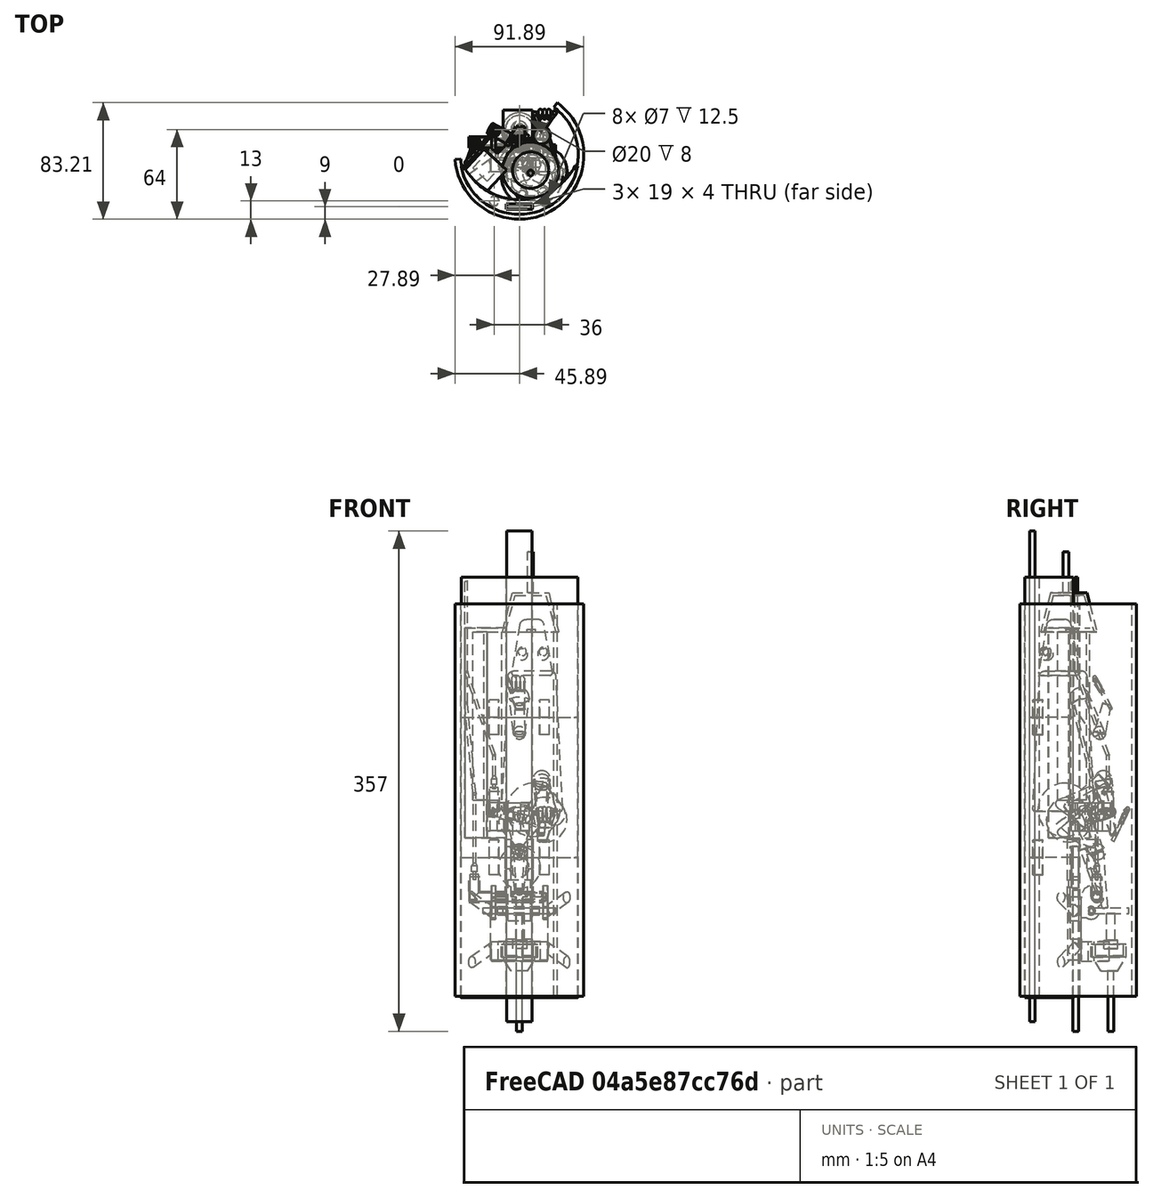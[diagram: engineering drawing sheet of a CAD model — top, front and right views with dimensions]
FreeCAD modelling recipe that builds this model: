
FCSTD DOCUMENT  (FreeCAD 0.19R17499 (Git))
Label: modele3.0
License: All rights reserved
LicenseURL: http://en.wikipedia.org/wiki/All_rights_reserved
objects: Part::Cylinder×80, Part::Cut×43, Part::Fuse×42, Part::Box×31, Part::Cone×19, Part::Sphere×19, Part::Fillet×16, Part::Mirroring×8, Part::MultiFuse×3, Drawing::FeatureViewPart×2, Drawing::FeaturePage×1
note: 261 computed .brp shape members not serialized (recipe doc carries the construction recipe); baked Part::Feature solids carry a one-line shape summary decoded from their .brp

FEATURE [Part::Cylinder] Cylinder  label="Cylindre"
  Angle = 360
  AttacherType = Attacher::AttachEngine3D
  Height = 100
  Radius = 42.5
FEATURE [Part::Cylinder] Cylinder001  label="Cylindre001"
  Angle = 360
  AttacherType = Attacher::AttachEngine3D
  Height = 100
  Placement = pos=(0,13,0) rot=(0,0,1;0rad)
  Radius = 45
FEATURE [Part::Cut] Cut
  Base = -> Cylinder
  Tool = -> Cylinder001
FEATURE [Part::Fillet] Fillet
  Base = -> Cut
  Edges = 1 edges r=1: [Edge4]
FEATURE [Part::Fillet] Fillet001
  Base = -> Fillet
  Edges = 1 edges r=1: [Edge3]
FEATURE [Part::Box] Box  label="Cube"
  AttacherType = Attacher::AttachEngine3D
  Height = 100
  Length = 19
  Placement = pos=(-9.5,-39,0) rot=(0,0,1;0rad)
  Width = 4
FEATURE [Part::Cut] Cut001  label="Support 1"
  Base = -> Fillet001
  Tool = -> Box
FEATURE [Part::Cylinder] Cylinder002  label="Cylindre002"
  Angle = 360
  AttacherType = Attacher::AttachEngine3D
  Height = 100
  Placement = pos=(0,13,0) rot=(0,0,1;0rad)
  Radius = 45
FEATURE [Part::Cylinder] Cylinder003  label="Cylindre003"
  Angle = 360
  AttacherType = Attacher::AttachEngine3D
  Height = 100
  Radius = 42.5
FEATURE [Part::Box] Box001  label="Cube001"
  AttacherType = Attacher::AttachEngine3D
  Height = 100
  Length = 19
  Placement = pos=(-9.5,-39,0) rot=(0,0,1;0rad)
  Width = 4
FEATURE [Part::Cut] Cut003
  Base = -> Cylinder003
  Tool = -> Cylinder002
FEATURE [Part::Fillet] Fillet003
  Base = -> Cut003
  Edges = 1 edges r=1: [Edge4]
FEATURE [Part::Fillet] Fillet002
  Base = -> Fillet003
  Edges = 1 edges r=1: [Edge3]
FEATURE [Part::Cut] Cut002  label="Support 2"
  Base = -> Fillet002
  Placement = pos=(0,0,-100) rot=(0,0,1;0rad)
  Tool = -> Box001
FEATURE [Part::Cylinder] Cylinder004  label="Cylindre004"
  Angle = 360
  AttacherType = Attacher::AttachEngine3D
  Height = 100
  Placement = pos=(0,13,0) rot=(0,0,1;0rad)
  Radius = 45
FEATURE [Part::Cylinder] Cylinder005  label="Cylindre005"
  Angle = 360
  AttacherType = Attacher::AttachEngine3D
  Height = 100
  Radius = 42.5
FEATURE [Part::Box] Box002  label="Cube002"
  AttacherType = Attacher::AttachEngine3D
  Height = 100
  Length = 19
  Placement = pos=(-9.5,-39,0) rot=(0,0,1;0rad)
  Width = 4
FEATURE [Part::Cut] Cut005
  Base = -> Cylinder005
  Tool = -> Cylinder004
FEATURE [Part::Fillet] Fillet005
  Base = -> Cut005
  Edges = 1 edges r=1: [Edge4]
FEATURE [Part::Fillet] Fillet004
  Base = -> Fillet005
  Edges = 1 edges r=1: [Edge3]
FEATURE [Part::Cut] Cut004  label="Support pedale"
  Base = -> Fillet004
  Placement = pos=(0,0,-200) rot=(0,0,1;0rad)
  Tool = -> Box002
FEATURE [Part::Cylinder] Cylinder006  label="Cylindre006"
  Angle = 360
  AttacherType = Attacher::AttachEngine3D
  Height = 25
  Placement = pos=(-18,-33,-12.5) rot=(0,0,1;0rad)
  Radius = 3.5
FEATURE [Part::Cylinder] Cylinder007  label="Cylindre007"
  Angle = 360
  AttacherType = Attacher::AttachEngine3D
  Height = 25
  Placement = pos=(-18,-33,-12.5) rot=(0,0,1;0rad)
  Radius = 3.5
FEATURE [Part::Cut] Cut006
  Base = -> Cut001
  Tool = -> Cylinder006
FEATURE [Part::Cut] Cut007
  Base = -> Cut002
  Tool = -> Cylinder007
FEATURE [Part::Cylinder] Cylinder009  label="Cylindre009"
  Angle = 360
  AttacherType = Attacher::AttachEngine3D
  Height = 25
  Placement = pos=(18,-33,-12.5) rot=(0,0,1;0rad)
  Radius = 3.5
FEATURE [Part::Cylinder] Cylinder010  label="Cylindre010"
  Angle = 360
  AttacherType = Attacher::AttachEngine3D
  Height = 25
  Placement = pos=(18,-33,-12.5) rot=(0,0,1;0rad)
  Radius = 3.5
FEATURE [Part::Cut] Cut008  label="Support 2 "
  Base = -> Cut007
  Tool = -> Cylinder009
FEATURE [Part::Cut] Cut009  label="Support 1 "
  Base = -> Cut006
  Tool = -> Cylinder010
FEATURE [Part::Cylinder] Cylinder011  label="Ergot 1"
  Angle = 360
  AttacherType = Attacher::AttachEngine3D
  Height = 25
  Placement = pos=(18,-33,-12.5) rot=(0,0,1;0rad)
  Radius = 3.3
FEATURE [Part::Cylinder] Cylinder012  label="Ergot 2"
  Angle = 360
  AttacherType = Attacher::AttachEngine3D
  Height = 25
  Placement = pos=(-18,-33,-12.5) rot=(0,0,1;0rad)
  Radius = 3.3
FEATURE [Part::Cylinder] Cylinder014  label="Cylindre012"
  Angle = 360
  AttacherType = Attacher::AttachEngine3D
  Height = 25
  Placement = pos=(-18,-33,-112.5) rot=(0,0,1;0rad)
  Radius = 3.5
FEATURE [Part::Cylinder] Cylinder015  label="Cylindre013"
  Angle = 360
  AttacherType = Attacher::AttachEngine3D
  Height = 25
  Placement = pos=(18,-33,-112.5) rot=(0,0,1;0rad)
  Radius = 3.5
FEATURE [Part::Cylinder] Cylinder016  label="Cylindre014"
  Angle = 360
  AttacherType = Attacher::AttachEngine3D
  Height = 25
  Placement = pos=(-18,-33,-112.5) rot=(0,0,1;0rad)
  Radius = 3.5
FEATURE [Part::Cylinder] Cylinder017  label="Cylindre015"
  Angle = 360
  AttacherType = Attacher::AttachEngine3D
  Height = 25
  Placement = pos=(18,-33,-112.5) rot=(0,0,1;0rad)
  Radius = 3.5
FEATURE [Part::Cut] Cut010
  Base = -> Cut008
  Tool = -> Cylinder016
FEATURE [Part::Cut] Cut011  label="Support 2 001"
  Base = -> Cut010
  Tool = -> Cylinder017
FEATURE [Part::Cut] Cut012
  Base = -> Cut004
  Tool = -> Cylinder014
FEATURE [Part::Cut] Cut013
  Base = -> Cut012
  Tool = -> Cylinder015
FEATURE [Part::Cylinder] Cylinder018  label="Ergot 3"
  Angle = 360
  AttacherType = Attacher::AttachEngine3D
  Height = 25
  Placement = pos=(18,-33,-112.5) rot=(0,0,1;0rad)
  Radius = 3.3
FEATURE [Part::Cylinder] Cylinder019  label="Ergot 4"
  Angle = 360
  AttacherType = Attacher::AttachEngine3D
  Height = 25
  Placement = pos=(-18,-33,-112.5) rot=(0,0,1;0rad)
  Radius = 3.3
FEATURE [Part::Box] Box003  label="Cube003"
  AttacherType = Attacher::AttachEngine3D
  Height = 45
  Length = 41
  Placement = pos=(-20.5,-12,-173) rot=(0,0,1;0rad)
  Width = 10
FEATURE [Part::Cylinder] Cylinder020  label="Cylindre016"
  Angle = 360
  AttacherType = Attacher::AttachEngine3D
  Height = 24
  Placement = pos=(-36,-18,-176) rot=(0,0.707107,0.707107;1.5708rad)
  Radius = 3.5
FEATURE [Part::Mirroring] Part__Mirroring  label="Cylindre016 (Mirror #1)"
  Base = (0,0,0)
  Normal = (0,0,1)
  Placement = pos=(0,0,-303) rot=(0,0,1;0rad)
  Source = -> Cylinder020
FEATURE [Part::Mirroring] Part__Mirroring001  label="Cylindre016 (Mirror #2)"
  Base = (0,0,0)
  Normal = (1,0,0)
  Source = -> Cylinder020
FEATURE [Part::Mirroring] Part__Mirroring002  label="Cylindre016 (Mirror #3)"
  Base = (0,0,0)
  Normal = (1,0,0)
  Source = -> Part__Mirroring
FEATURE [Part::Fuse] Fusion
  Base = -> Box003
  Tool = -> Cylinder020
FEATURE [Part::Fuse] Fusion001
  Base = -> Part__Mirroring
  Tool = -> Fusion
FEATURE [Part::Fuse] Fusion002
  Base = -> Part__Mirroring002
  Tool = -> Fusion001
FEATURE [Part::Fuse] Fusion003
  Base = -> Part__Mirroring001
  Tool = -> Fusion002
FEATURE [Part::Fuse] Fusion004
  Base = -> Cut013
  Tool = -> Fusion003
FEATURE [Part::Cylinder] Cylinder021  label="Cylindre017"
  Angle = 360
  AttacherType = Attacher::AttachEngine3D
  Height = 30
  Placement = pos=(-13,6,-138) rot=(0,1,0;1.5708rad)
  Radius = 3
FEATURE [Part::Box] Box004  label="Cube004"
  AttacherType = Attacher::AttachEngine3D
  Height = 30
  Length = 18
  Placement = pos=(-9,-10,-158) rot=(0,0,1;0rad)
  Width = 8
FEATURE [Part::Cut] Cut014
  Base = -> Fusion004
  Tool = -> Box004
FEATURE [Part::Box] Box005  label="Cube005"
  AttacherType = Attacher::AttachEngine3D
  Height = 51
  Length = 5
  Placement = pos=(-2.5,-14,-174) rot=(0,0,1;0rad)
  Width = 14
FEATURE [Part::Cut] Cut015
  Base = -> Cut014
  Tool = -> Box005
FEATURE [Part::Cylinder] Cylinder022  label="Cylindre018"
  Angle = 360
  AttacherType = Attacher::AttachEngine3D
  Height = 34
  Placement = pos=(-17,6,-138) rot=(0,1,0;1.5708rad)
  Radius = 7
FEATURE [Part::Cylinder] Cylinder024  label="Cylindre020"
  Angle = 360
  AttacherType = Attacher::AttachEngine3D
  Height = 40
  Placement = pos=(-20,6,-138) rot=(0,1,0;1.5708rad)
  Radius = 6
FEATURE [Part::Cylinder] Cylinder025  label="Cylindre021"
  Angle = 360
  AttacherType = Attacher::AttachEngine3D
  Height = 48
  Placement = pos=(-26,6,-138) rot=(0,1,0;1.5708rad)
  Radius = 2
FEATURE [Part::Cut] Cut017
  Base = -> Cylinder024
  Tool = -> Cylinder025
FEATURE [Part::Cylinder] Cylinder026  label="Cylindre022"
  Angle = 360
  AttacherType = Attacher::AttachEngine3D
  Height = 52
  Placement = pos=(-26,6,-138) rot=(0,1,0;1.5708rad)
  Radius = 1.5
FEATURE [Part::Cut] Cut018
  Base = -> Cut017
  Placement = pos=(0,-1,0) rot=(0,0,1;0rad)
  Tool = -> Cylinder022
FEATURE [Part::Cylinder] Cylinder027  label="Cylindre023"
  Angle = 360
  AttacherType = Attacher::AttachEngine3D
  Height = 34
  Placement = pos=(-17,6,-128) rot=(0,1,0;1.5708rad)
  Radius = 8
FEATURE [Part::Cylinder] Cylinder028  label="Axe pedale"
  Angle = 360
  AttacherType = Attacher::AttachEngine3D
  Height = 52
  Placement = pos=(-26,5,-138) rot=(0,1,0;1.5708rad)
  Radius = 2
FEATURE [Part::Cut] Cut019
  Base = -> Cylinder021
  Placement = pos=(0,-1,0) rot=(0,0,1;0rad)
  Tool = -> Cylinder026
FEATURE [Part::Cylinder] Cylinder029  label="Cylindre025"
  Angle = 360
  AttacherType = Attacher::AttachEngine3D
  Height = 40
  Placement = pos=(-20,6,-128) rot=(0,1,0;1.5708rad)
  Radius = 8
FEATURE [Part::Cut] Cut020
  Base = -> Cylinder029
  Tool = -> Cylinder027
FEATURE [Part::Box] Box006  label="Cube006"
  AttacherType = Attacher::AttachEngine3D
  Height = 4
  Length = 21
  Placement = pos=(-9,7,-140) rot=(0,0,1;0rad)
  Width = 25
FEATURE [Part::Fuse] Fusion005
  Base = -> Cut019
  Tool = -> Box006
FEATURE [Part::Cylinder] Cylinder030  label="Cylindre026"
  Angle = 360
  AttacherType = Attacher::AttachEngine3D
  Height = 52
  Placement = pos=(-26,9,-128) rot=(0,1,0;1.5708rad)
  Radius = 2.5
FEATURE [Part::Cylinder] Cylinder031  label="Cylindre027"
  Angle = 360
  AttacherType = Attacher::AttachEngine3D
  Height = 21
  Placement = pos=(3,19,-161) rot=(0,0,1;0rad)
  Radius = 3
FEATURE [Part::Cylinder] Cylinder032  label="Cylindre028"
  Angle = 360
  AttacherType = Attacher::AttachEngine3D
  Height = 6
  Placement = pos=(3,19,-165) rot=(0,0,1;0rad)
  Radius = 5
FEATURE [Part::Fuse] Fusion006
  Base = -> Fusion005
  Tool = -> Cylinder031
FEATURE [Part::Fuse] Fusion007  label="Pedale"
  Base = -> Cylinder032
  Placement = pos=(-2.5,0,0) rot=(0,0,1;0rad)
  Tool = -> Fusion006
FEATURE [Part::Box] Box007  label="Cube007"
  AttacherType = Attacher::AttachEngine3D
  Height = 14
  Length = 3
  Placement = pos=(17,-2,-143) rot=(0,0,1;0rad)
  Width = 5
FEATURE [Part::Box] Box008  label="Cube008"
  AttacherType = Attacher::AttachEngine3D
  Height = 14
  Length = 3
  Placement = pos=(-20,-2,-143) rot=(0,0,1;0rad)
  Width = 5
FEATURE [Part::Cylinder] Cylinder033  label="Cylindre029"
  Angle = 360
  AttacherType = Attacher::AttachEngine3D
  Height = 52
  Placement = pos=(-26,9,-128) rot=(0,1,0;1.5708rad)
  Radius = 2.5
FEATURE [Part::Cut] Cut021
  Base = -> Cut020
  Tool = -> Cylinder030
FEATURE [Part::Cut] Cut022
  Base = -> Cut021
  Tool = -> Cylinder033
FEATURE [Part::Cylinder] Cylinder034  label="Cylindre030"
  Angle = 360
  AttacherType = Attacher::AttachEngine3D
  Height = 38
  Placement = pos=(-20,9,-128) rot=(0,1,0;1.5708rad)
  Radius = 4
FEATURE [Part::Cylinder] Cylinder035  label="Cylindre031"
  Angle = 360
  AttacherType = Attacher::AttachEngine3D
  Height = 38
  Placement = pos=(-20,9,-128) rot=(0,1,0;1.5708rad)
  Radius = 2.5
FEATURE [Part::Cut] Cut023
  Base = -> Cylinder034
  Tool = -> Cylinder035
FEATURE [Part::Box] Box009  label="Cube009"
  AttacherType = Attacher::AttachEngine3D
  Height = 10
  Length = 34
  Placement = pos=(-17,11,-133) rot=(0,0,1;0rad)
  Width = 5
FEATURE [Part::Cut] Cut024
  Base = -> Cut023
  Tool = -> Box009
FEATURE [Part::Cylinder] Cylinder036  label="Cylindre032"
  Angle = 360
  AttacherType = Attacher::AttachEngine3D
  Height = 10
  Placement = pos=(0,12,-133) rot=(0,0,1;0rad)
  Radius = 4
FEATURE [Part::Cut] Cut025
  Base = -> Cut024
  Tool = -> Cylinder036
FEATURE [Part::Fuse] Fusion008
  Base = -> Cut022
  Tool = -> Cut025
FEATURE [Part::Fuse] Fusion009
  Base = -> Cut018
  Tool = -> Fusion008
FEATURE [Part::Fuse] Fusion010
  Base = -> Box007
  Tool = -> Fusion009
FEATURE [Part::Fuse] Fusion011
  Base = -> Box008
  Tool = -> Fusion010
FEATURE [Part::Fuse] Fusion012
  Base = -> Cut015
  Tool = -> Fusion011
FEATURE [Part::Cylinder] Cylinder037  label="Cylindre033"
  Angle = 360
  AttacherType = Attacher::AttachEngine3D
  Height = 18
  Placement = pos=(-36,9,-128) rot=(0,1,0;1.5708rad)
  Radius = 4
FEATURE [Part::Cylinder] Cylinder038  label="Cylindre034"
  Angle = 360
  AttacherType = Attacher::AttachEngine3D
  Height = 18
  Placement = pos=(-36,9,-128) rot=(0,1,0;1.5708rad)
  Radius = 3
FEATURE [Part::Cut] Cut026
  Base = -> Cylinder037
  Tool = -> Cylinder038
FEATURE [Part::Cylinder] Cylinder041  label="Cylindre037"
  Angle = 360
  AttacherType = Attacher::AttachEngine3D
  Height = 14
  Placement = pos=(-32,9,-128) rot=(0,0,1;0rad)
  Radius = 4
FEATURE [Part::Cylinder] Cylinder042  label="Cylindre038"
  Angle = 360
  AttacherType = Attacher::AttachEngine3D
  Height = 16
  Placement = pos=(-32,9,-129) rot=(0,0,1;0rad)
  Radius = 3
FEATURE [Part::Cylinder] Cylinder043  label="Cylindre039"
  Angle = 360
  AttacherType = Attacher::AttachEngine3D
  Height = 26
  Placement = pos=(-42,9,-128) rot=(0,1,0;1.5708rad)
  Radius = 3
FEATURE [Part::Cut] Cut028
  Base = -> Cylinder041
  Tool = -> Cylinder042
FEATURE [Part::Cut] Cut029
  Base = -> Cut028
  Tool = -> Cylinder043
FEATURE [Part::Fuse] Fusion013
  Base = -> Cut026
  Tool = -> Cut029
FEATURE [Part::Fuse] Fusion014
  Base = -> Fusion012
  Tool = -> Fusion013
FEATURE [Part::Cylinder] Cylinder044  label="Cylindre040"
  Angle = 360
  AttacherType = Attacher::AttachEngine3D
  Height = 10
  Placement = pos=(-32,9,-127) rot=(0,0,1;0rad)
  Radius = 3
FEATURE [Part::Cut] Cut030
  Base = -> Fusion014
  Tool = -> Cylinder044
FEATURE [Part::Box] Box010  label="Cube010"
  AttacherType = Attacher::AttachEngine3D
  Height = 43
  Length = 4
  Placement = pos=(6,-12,-130) rot=(0,0,1;0rad)
  Width = 2
FEATURE [Part::Box] Box011  label="Cube011"
  AttacherType = Attacher::AttachEngine3D
  Height = 21
  Length = 4
  Placement = pos=(-10,2,-108) rot=(0,0,1;0rad)
  Width = 6
FEATURE [Part::Box] Box012  label="Cube012"
  AttacherType = Attacher::AttachEngine3D
  Height = 5
  Length = 4
  Placement = pos=(-10,-12,-92) rot=(0,0,1;0rad)
  Width = 20
FEATURE [Part::Box] Box013  label="Cube013"
  AttacherType = Attacher::AttachEngine3D
  Height = 5
  Length = 4
  Placement = pos=(6,-12,-92) rot=(0,0,1;0rad)
  Width = 20
FEATURE [Part::Box] Box014  label="Cube014"
  AttacherType = Attacher::AttachEngine3D
  Height = 43
  Length = 4
  Placement = pos=(-10,-12,-130) rot=(0,0,1;0rad)
  Width = 2
FEATURE [Part::Box] Box015  label="Cube015"
  AttacherType = Attacher::AttachEngine3D
  Height = 21
  Length = 4
  Placement = pos=(6,2,-108) rot=(0,0,1;0rad)
  Width = 6
FEATURE [Part::Fuse] Fusion015
  Base = -> Box011
  Tool = -> Box012
FEATURE [Part::Fuse] Fusion016
  Base = -> Box014
  Tool = -> Fusion015
FEATURE [Part::Fuse] Fusion017
  Base = -> Cut030
  Tool = -> Fusion016
FEATURE [Part::Fuse] Fusion018
  Base = -> Box015
  Tool = -> Fusion017
FEATURE [Part::MultiFuse] Fusion019
  Shapes = -> [Fusion018,Box013]
FEATURE [Part::Fuse] Fusion020
  Base = -> Box010
  Tool = -> Fusion019
FEATURE [Part::Box] Box016  label="Cube016"
  AttacherType = Attacher::AttachEngine3D
  Height = 14
  Length = 40
  Placement = pos=(-20,-2,-174) rot=(0,0,1;0rad)
  Width = 20
FEATURE [Part::Cylinder] Cylinder045  label="Cylindre041"
  Angle = 360
  AttacherType = Attacher::AttachEngine3D
  Height = 15
  Placement = pos=(0,18,-174) rot=(0,0,1;0rad)
  Radius = 11
FEATURE [Part::Cut] Cut031
  Base = -> Box016
  Tool = -> Cylinder045
FEATURE [Part::Cylinder] Cylinder046  label="Cylindre042"
  Angle = 360
  AttacherType = Attacher::AttachEngine3D
  Height = 9
  Placement = pos=(0,18,-171) rot=(0,0,1;0rad)
  Radius = 13
FEATURE [Part::Cut] Cut032
  Base = -> Cut031
  Tool = -> Cylinder046
FEATURE [Part::Box] Box017  label="Cube017"
  AttacherType = Attacher::AttachEngine3D
  Height = 16
  Length = 30
  Placement = pos=(-15,-2,-175) rot=(0,0,1;0rad)
  Width = 5
FEATURE [Part::Cut] Cut033
  Base = -> Cut032
  Tool = -> Box017
FEATURE [Part::Fuse] Fusion021  label="Support antenne/pedale"
  Base = -> Fusion020
  Tool = -> Cut033
FEATURE [Part::Box] Box018  label="Cube018"
  AttacherType = Attacher::AttachEngine3D
  Height = 150
  Length = 20
  Placement = pos=(-19.7,-27.5,0) rot=(0,0,1;0.820305rad)
  Width = 22
FEATURE [Part::Cylinder] Cylinder047  label="Cylindre043"
  Angle = 360
  AttacherType = Attacher::AttachEngine3D
  Height = 150
  Placement = pos=(2,12,0) rot=(0,0,1;0rad)
  Radius = 45
FEATURE [Part::Box] Box019  label="Cube019"
  AttacherType = Attacher::AttachEngine3D
  Height = 150
  Length = 200
  Placement = pos=(12,-57,0) rot=(0,0,1;0.820305rad)
  Width = 200
FEATURE [Part::Cut] Cut034
  Base = -> Cylinder047
  Tool = -> Box019
FEATURE [Part::Fuse] Fusion022
  Base = -> Box018
  Placement = pos=(-3,2,-86) rot=(0,0,1;0rad)
  Tool = -> Cut034
FEATURE [Part::Box] Box020  label="Cube020"
  AttacherType = Attacher::AttachEngine3D
  Height = 120
  Length = 16
  Placement = pos=(-23,-19,-59) rot=(0,0,1;0.820305rad)
  Width = 14
FEATURE [Part::Cut] Cut035
  Base = -> Fusion022
  Tool = -> Box020
FEATURE [Part::Box] Box021  label="Cube021"
  AttacherType = Attacher::AttachEngine3D
  Height = 20
  Length = 4
  Placement = pos=(-11,-9,-81) rot=(0,0,1;0.820305rad)
  Width = 17
FEATURE [Part::Box] Box022  label="Cube022"
  AttacherType = Attacher::AttachEngine3D
  Height = 20
  Length = 25
  Placement = pos=(-10,-5,-81) rot=(0,0,1;0.820305rad)
  Width = 8
FEATURE [Part::Fuse] Fusion023
  Base = -> Box021
  Tool = -> Box022
FEATURE [Part::Cylinder] Cylinder048  label="Cylindre044"
  Angle = 360
  AttacherType = Attacher::AttachEngine3D
  Height = 8
  Placement = pos=(0,18,-170) rot=(0,0,1;0rad)
  Radius = 10
FEATURE [Part::Cylinder] Cylinder049  label="Cylindre045"
  Angle = 360
  AttacherType = Attacher::AttachEngine3D
  Height = 9
  Placement = pos=(0,18,-171) rot=(0,0,1;0rad)
  Radius = 12
FEATURE [Part::Cut] Cut036
  Base = -> Cylinder049
  Tool = -> Cylinder048
FEATURE [Part::Cone] Cone  label="Cône"
  Angle = 360
  AttacherType = Attacher::AttachEngine3D
  Height = 10
  Placement = pos=(0,18,-181) rot=(0,0,1;0rad)
  Radius1 = 6
  Radius2 = 12
FEATURE [Part::Fuse] Fusion024  label="Capteur pression"
  Base = -> Cut036
  Tool = -> Cone
FEATURE [Part::Cylinder] Cylinder050  label="Cylindre046"
  Angle = 360
  AttacherType = Attacher::AttachEngine3D
  Height = 51
  Placement = pos=(-32,9,-128) rot=(0,1,0;1.5708rad)
  Radius = 3
FEATURE [Part::Cylinder] Cylinder051  label="Cylindre047"
  Angle = 360
  AttacherType = Attacher::AttachEngine3D
  Height = 18
  Placement = pos=(-32,9,-130) rot=(0,0,1;0rad)
  Radius = 3
FEATURE [Part::Fuse] Fusion025  label="Electrode 1"
  Base = -> Cylinder050
  Tool = -> Cylinder051
FEATURE [Part::Cylinder] Cylinder052  label="Cylindre048"
  Angle = 360
  AttacherType = Attacher::AttachEngine3D
  Height = 4
  Placement = pos=(-32,9,-110) rot=(0,0,1;0rad)
  Radius = 2
FEATURE [Part::Cylinder] Cylinder053  label="Cylindre049"
  Angle = 360
  AttacherType = Attacher::AttachEngine3D
  Height = 8
  Placement = pos=(-32,9,-116) rot=(0,0,1;0rad)
  Radius = 1
FEATURE [Part::Cone] Cone001  label="Cône001"
  Angle = 360
  AttacherType = Attacher::AttachEngine3D
  Height = 2
  Placement = pos=(-32,9,-106) rot=(0,0,1;0rad)
  Radius1 = 2
  Radius2 = 1
FEATURE [Part::Cylinder] Cylinder054  label="Cylindre050"
  Angle = 360
  AttacherType = Attacher::AttachEngine3D
  Height = 50
  Placement = pos=(-32,9,-104) rot=(0,0,1;0rad)
  Radius = 1
FEATURE [Part::Fuse] Fusion026
  Base = -> Cylinder052
  Tool = -> Cone001
FEATURE [Part::Cylinder] Cylinder055  label="Cylindre051"
  Angle = 360
  AttacherType = Attacher::AttachEngine3D
  Height = 23
  Placement = pos=(-3,6,-72) rot=(-0.727607,-0.485071,0.485071;1.65806rad)
  Radius = 4
FEATURE [Part::Cylinder] Cylinder056  label="Cylindre052"
  Angle = 360
  AttacherType = Attacher::AttachEngine3D
  Height = 20
  Placement = pos=(3,6,-72) rot=(-0.725865,-0.488827,0.48391;1.65806rad)
  Radius = 3
FEATURE [Part::Cylinder] Cylinder057  label="Cylindre053"
  Angle = 360
  AttacherType = Attacher::AttachEngine3D
  Height = 25
  Placement = pos=(-3,6,-72) rot=(-0.725865,-0.488827,0.48391;1.65806rad)
  Radius = 3
FEATURE [Part::Cut] Cut037
  Base = -> Fusion023
  Tool = -> Cylinder056
FEATURE [Part::Cut] Cut038
  Base = -> Cylinder055
  Placement = pos=(2,2,1) rot=(0,0,1;0rad)
  Tool = -> Cylinder057
FEATURE [Part::Cylinder] Cylinder058  label="Cylindre054"
  Angle = 360
  AttacherType = Attacher::AttachEngine3D
  Height = 14
  Placement = pos=(-18,17,-67) rot=(0,0,1;0rad)
  Radius = 3
FEATURE [Part::Cylinder] Cylinder059  label="Cylindre055"
  Angle = 360
  AttacherType = Attacher::AttachEngine3D
  Height = 14
  Placement = pos=(-18,17,-67) rot=(0,0,1;0rad)
  Radius = 4
FEATURE [Part::Fuse] Fusion027
  Base = -> Cut038
  Tool = -> Cylinder059
FEATURE [Part::Cut] Cut039
  Base = -> Fusion027
  Tool = -> Cylinder058
FEATURE [Part::Fuse] Fusion028
  Base = -> Cut037
  Tool = -> Cut039
FEATURE [Part::Cylinder] Cylinder060  label="Cylindre056"
  Angle = 360
  AttacherType = Attacher::AttachEngine3D
  Height = 30
  Placement = pos=(6,4,-73) rot=(-0.725265,-0.486822,0.486822;1.65806rad)
  Radius = 3
FEATURE [Part::Cylinder] Cylinder061  label="Cylindre057"
  Angle = 360
  AttacherType = Attacher::AttachEngine3D
  Height = 20
  Placement = pos=(-18,17,-70) rot=(0,0,1;0rad)
  Radius = 3
FEATURE [Part::Cylinder] Cylinder062  label="Cylindre058"
  Angle = 360
  AttacherType = Attacher::AttachEngine3D
  Height = 4
  Placement = pos=(-32,9,-110) rot=(0,0,1;0rad)
  Radius = 2
FEATURE [Part::Cone] Cone002  label="Cône002"
  Angle = 360
  AttacherType = Attacher::AttachEngine3D
  Height = 2
  Placement = pos=(-32,9,-106) rot=(0,0,1;0rad)
  Radius1 = 2
  Radius2 = 1
FEATURE [Part::Fuse] Fusion029
  Base = -> Cylinder062
  Placement = pos=(14,8,62) rot=(0,0,1;0rad)
  Tool = -> Cone002
FEATURE [Part::Cylinder] Cylinder064  label="Cylindre060"
  Angle = 360
  AttacherType = Attacher::AttachEngine3D
  Height = 8
  Placement = pos=(-18,17,-51) rot=(0,0,1;0rad)
  Radius = 1
FEATURE [Part::Cylinder] Cylinder065  label="Cylindre061"
  Angle = 360
  AttacherType = Attacher::AttachEngine3D
  Height = 87
  Placement = pos=(-38,-8.4,10) rot=(0,0,1;0rad)
  Radius = 1
FEATURE [Part::Fuse] Fusion030  label="Electrode 2"
  Base = -> Cylinder060
  Tool = -> Cylinder061
FEATURE [Part::Cylinder] Cylinder066  label="Cylindre062"
  Angle = 360
  AttacherType = Attacher::AttachEngine3D
  Height = 5
  Placement = pos=(0,-4,-107) rot=(1,0,0;1.5708rad)
  Radius = 7
FEATURE [Part::Cylinder] Cylinder067  label="Cylindre063"
  Angle = 360
  AttacherType = Attacher::AttachEngine3D
  Height = 5
  Placement = pos=(0,-4,-107) rot=(1,0,0;1.5708rad)
  Radius = 15
FEATURE [Part::Cut] Cut040
  Base = -> Cylinder067
  Tool = -> Cylinder066
FEATURE [Part::Box] Box023  label="Cube023"
  AttacherType = Attacher::AttachEngine3D
  Height = 29
  Length = 16
  Placement = pos=(-8,-11,-145) rot=(0,0,1;0rad)
  Width = 7.5
FEATURE [Part::Cylinder] Cylinder068  label="Cylindre064"
  Angle = 360
  AttacherType = Attacher::AttachEngine3D
  Height = 68
  Placement = pos=(-32,9,-55) rot=(0.666667,-0.333333,0.666667;0.366519rad)
  Radius = 1
FEATURE [Part::Fuse] Fusion031
  Base = -> Cylinder054
  Tool = -> Cylinder068
FEATURE [Part::Cylinder] Cylinder069  label="Cylindre065"
  Angle = 360
  AttacherType = Attacher::AttachEngine3D
  Height = 67
  Placement = pos=(-18,17,-27) rot=(0.539164,-0.646997,0.539164;0.558505rad)
  Radius = 1
FEATURE [Part::Cylinder] Cylinder070  label="Cylindre066"
  Angle = 360
  AttacherType = Attacher::AttachEngine3D
  Height = 68
  Placement = pos=(-38,-5.6,32) rot=(0,0,1;0rad)
  Radius = 1
FEATURE [Part::Cylinder] Cylinder071  label="Cylindre067"
  Angle = 360
  AttacherType = Attacher::AttachEngine3D
  Height = 16
  Placement = pos=(-18,17,-43) rot=(0,0,1;0rad)
  Radius = 1
FEATURE [Part::Fillet] Fillet006
  Base = -> Cut040
  Edges = 1 edges r=1: [Edge3]
FEATURE [Part::Fillet] Fillet007
  Base = -> Fillet006
  Edges = 1 edges r=1: [Edge3]
FEATURE [Part::Fuse] Fusion032
  Base = -> Cylinder065
  Tool = -> Fusion031
FEATURE [Part::Fuse] Fusion033
  Base = -> Fusion026
  Tool = -> Fusion032
FEATURE [Part::Fuse] Fusion034  label="Fil 1"
  Base = -> Cylinder053
  Tool = -> Fusion033
FEATURE [Part::Fuse] Fusion035
  Base = -> Fusion029
  Tool = -> Cylinder071
FEATURE [Part::Fuse] Fusion036
  Base = -> Cylinder064
  Tool = -> Fusion035
FEATURE [Part::Fuse] Fusion037
  Base = -> Cylinder069
  Tool = -> Fusion036
FEATURE [Part::Fuse] Fusion038  label="Fil 2"
  Base = -> Cylinder070
  Tool = -> Fusion037
FEATURE [Part::Cylinder] Cylinder072  label="Cylindre068"
  Angle = 360
  AttacherType = Attacher::AttachEngine3D
  Height = 297
  Placement = pos=(0,0,-207) rot=(0,0,1;0rad)
  Radius = 42
FEATURE [Part::Cylinder] Cylinder073  label="Cylindre069"
  Angle = 230
  AttacherType = Attacher::AttachEngine3D
  Height = 280
  Placement = pos=(0,0,-207) rot=(0,0,1;3.21141rad)
  Radius = 46
FEATURE [Part::Cut] Cut041  label="Antenne d'émission"
  Base = -> Cylinder073
  Placement = pos=(0,0,8) rot=(0,0,1;0rad)
  Tool = -> Cylinder072
FEATURE [Part::Box] Box024  label="Cube024"
  AttacherType = Attacher::AttachEngine3D
  Height = 350
  Length = 18
  Placement = pos=(-9,-39,-217) rot=(0,0,1;0rad)
  Width = 4
FEATURE [Part::Cone] Cone003  label="Cône003"
  Angle = 360
  AttacherType = Attacher::AttachEngine3D
  Height = 100
  Placement = pos=(7,-12,-84) rot=(0,0,1;0rad)
  Radius1 = 22
  Radius2 = 17
FEATURE [Part::Cone] Cone004  label="Cône004"
  Angle = 360
  AttacherType = Attacher::AttachEngine3D
  Height = 34
  Placement = pos=(0,11,-111) rot=(0.707107,0,0.707107;0.575959rad)
  Radius1 = 5
  Radius2 = 7
FEATURE [Part::Cone] Cone005  label="Cône005"
  Angle = 360
  AttacherType = Attacher::AttachEngine3D
  Height = 40
  Placement = pos=(0,15,-136) rot=(1,0,0;0.174533rad)
  Radius1 = 2
  Radius2 = 6
FEATURE [Part::Fillet] Fillet008
  Base = -> Cone003
  Edges = 1 edges r=2: [Edge3]
  Placement = pos=(2,-3,17) rot=(1,0,0;0rad)
FEATURE [Part::Fillet] Fillet009
  Base = -> Cone004
  Edges = 1 edges r=2: [Edge1]
  Placement = pos=(16,-85,-96) rot=(1,0,0;1.95477rad)
FEATURE [Part::Sphere] Sphere  label="Sphère"
  Angle1 = -90
  Angle2 = 90
  Angle3 = 360
  AttacherType = Attacher::AttachEngine3D
  Placement = pos=(0,9.7,-96) rot=(0,0,1;0rad)
  Radius = 5.5
FEATURE [Part::Box] Box025  label="Cube025"
  AttacherType = Attacher::AttachEngine3D
  Height = 2
  Length = 11
  Placement = pos=(-7,12,-136) rot=(0,0,1;0rad)
  Width = 22
FEATURE [Part::Box] Box026  label="Cube026"
  AttacherType = Attacher::AttachEngine3D
  Height = 10
  Length = 10
  Placement = pos=(-12,9,-144) rot=(0,0,1;0.279253rad)
  Width = 19
FEATURE [Part::Cut] Cut042
  Base = -> Box025
  Tool = -> Box026
FEATURE [Part::Cylinder] Cylinder074  label="Cylindre070"
  Angle = 360
  AttacherType = Attacher::AttachEngine3D
  Height = 10
  Placement = pos=(-4,37,-135) rot=(1,0,0;1.5708rad)
  Radius = 1.5
FEATURE [Part::Cylinder] Cylinder075  label="Cylindre071"
  Angle = 360
  AttacherType = Attacher::AttachEngine3D
  Height = 10
  Placement = pos=(-1,37,-135) rot=(1,0,0;1.5708rad)
  Radius = 1.5
FEATURE [Part::Cylinder] Cylinder076  label="Cylindre072"
  Angle = 360
  AttacherType = Attacher::AttachEngine3D
  Height = 10
  Placement = pos=(-5,26,-135) rot=(-0.948683,0,0.316228;1.62316rad)
  Radius = 1.5
FEATURE [Part::Cylinder] Cylinder077  label="Cylindre073"
  Angle = 360
  AttacherType = Attacher::AttachEngine3D
  Height = 17
  Placement = pos=(6,33,-135) rot=(0.980581,-0.196116,0;1.53589rad)
  Radius = 1.5
FEATURE [Part::Cylinder] Cylinder078  label="Cylindre074"
  Angle = 360
  AttacherType = Attacher::AttachEngine3D
  Height = 10
  Placement = pos=(2,37,-135) rot=(1,0,0;1.5708rad)
  Radius = 1.5
FEATURE [Part::Sphere] Sphere001  label="Sphère001"
  Angle1 = -90
  Angle2 = 90
  Angle3 = 360
  AttacherType = Attacher::AttachEngine3D
  Placement = pos=(2,37,-135) rot=(0,0,1;0rad)
  Radius = 1.5
FEATURE [Part::Sphere] Sphere002  label="Sphère002"
  Angle1 = -90
  Angle2 = 90
  Angle3 = 360
  AttacherType = Attacher::AttachEngine3D
  Placement = pos=(-1,37,-135) rot=(0,0,1;0rad)
  Radius = 1.5
FEATURE [Part::Sphere] Sphere003  label="Sphère003"
  Angle1 = -90
  Angle2 = 90
  Angle3 = 360
  AttacherType = Attacher::AttachEngine3D
  Placement = pos=(-4,37,-135) rot=(0,0,1;0rad)
  Radius = 1.5
FEATURE [Part::Sphere] Sphere004  label="Sphère004"
  Angle1 = -90
  Angle2 = 90
  Angle3 = 360
  AttacherType = Attacher::AttachEngine3D
  Placement = pos=(-8.15,35.5,-134.5) rot=(0,0,1;0rad)
  Radius = 1.5
FEATURE [Part::Sphere] Sphere005  label="Sphère005"
  Angle1 = -90
  Angle2 = 90
  Angle3 = 360
  AttacherType = Attacher::AttachEngine3D
  Placement = pos=(6,33,-135) rot=(0,0,1;0rad)
  Radius = 1.5
FEATURE [Part::MultiFuse] Fusion040
  Shapes = -> [Cut042,Cylinder076,Sphere004,Cylinder074,Sphere003,Cylinder075,Sphere002,Cylinder078,Sphere001,Cylinder077,Sphere005]
FEATURE [Part::Mirroring] Part__Mirroring003  label="Fusion040 (Mirror #4)"
  Base = (0,0,0)
  Normal = (1,0,0)
  Placement = pos=(17,-107,-42) rot=(1,0,0;1.13446rad)
  Source = -> Fusion040
FEATURE [Part::Cone] Cone006  label="Cône006"
  Angle = 360
  AttacherType = Attacher::AttachEngine3D
  Height = 34
  Placement = pos=(16,21,-83) rot=(1,0,0;0.296706rad)
  Radius1 = 2
  Radius2 = 4
FEATURE [Part::Cone] Cone007  label="Cône007"
  Angle = 360
  AttacherType = Attacher::AttachEngine3D
  Height = 26
  Placement = pos=(0,8,-92) rot=(1,0,0;0.698132rad)
  Radius1 = 2
  Radius2 = 17
FEATURE [Part::Cone] Cone008  label="Cône008"
  Angle = 360
  AttacherType = Attacher::AttachEngine3D
  Height = 34
  Placement = pos=(18,17,-48) rot=(1,0,0;2.32129rad)
  Radius1 = 2
  Radius2 = 10
FEATURE [Part::Sphere] Sphere006  label="Sphère006"
  Angle1 = -90
  Angle2 = 90
  Angle3 = 360
  AttacherType = Attacher::AttachEngine3D
  Placement = pos=(10,-14,-66) rot=(0,0,1;0rad)
  Radius = 19
FEATURE [Part::Fillet] Fillet010
  Base = -> Cone007
  Edges = 1 edges r=3: [Edge1]
FEATURE [Part::Cone] Cone009  label="Cône009"
  Angle = 360
  AttacherType = Attacher::AttachEngine3D
  Height = 26
  Placement = pos=(0,8,-92) rot=(1,0,0;0.698132rad)
  Radius1 = 2
  Radius2 = 17
FEATURE [Part::Fillet] Fillet011
  Base = -> Cone009
  Edges = 1 edges r=3: [Edge1]
  Placement = pos=(18,-82,-79) rot=(1,0,0;1.79769rad)
FEATURE [Part::Cone] Cone010  label="Cône010"
  Angle = 360
  AttacherType = Attacher::AttachEngine3D
  Height = 34
  Placement = pos=(0,11,-111) rot=(0.707107,0,0.707107;0.575959rad)
  Radius1 = 5
  Radius2 = 7
FEATURE [Part::Fillet] Fillet012
  Base = -> Cone010
  Edges = 1 edges r=2: [Edge1]
  Placement = pos=(0,-2,15) rot=(0,0,1;0rad)
FEATURE [Part::Cone] Cone011  label="Cône011"
  Angle = 360
  AttacherType = Attacher::AttachEngine3D
  Height = 34
  Placement = pos=(0,8,-98) rot=(1,0,0;0.610865rad)
  Radius1 = 2
  Radius2 = 10
FEATURE [Part::Sphere] Sphere007  label="Sphère007"
  Angle1 = -90
  Angle2 = 90
  Angle3 = 360
  AttacherType = Attacher::AttachEngine3D
  Placement = pos=(16,13.7,-44) rot=(0,0,1;0rad)
  Radius = 6
FEATURE [Part::Sphere] Sphere008  label="Sphère008"
  Angle1 = -90
  Angle2 = 90
  Angle3 = 360
  AttacherType = Attacher::AttachEngine3D
  Placement = pos=(18,-11,-73) rot=(0,0,1;0rad)
  Radius = 16
FEATURE [Part::Cone] Cone012  label="Cône012"
  Angle = 360
  AttacherType = Attacher::AttachEngine3D
  Height = 40
  Placement = pos=(16,21,-84) rot=(1,0,0;0.174533rad)
  Radius1 = 2
  Radius2 = 6
FEATURE [Part::Cone] Cone013  label="Cône013"
  Angle = 360
  AttacherType = Attacher::AttachEngine3D
  Height = 34
  Placement = pos=(0,11,-126) rot=(1,0,0;0.296706rad)
  Radius1 = 2
  Radius2 = 4
FEATURE [Part::Fillet] Fillet013
  Base = -> Fillet008
  Edges = 1 edges r=4: [Edge3]
FEATURE [Part::Cone] Cone014  label="Cône014"
  Angle = 360
  AttacherType = Attacher::AttachEngine3D
  Height = 40
  Placement = pos=(10,-18,16) rot=(0,0,1;0rad)
  Radius1 = 15
  Radius2 = 8
FEATURE [Part::Fillet] Fillet014
  Base = -> Cone014
  Edges = 1 edges r=2: [Edge3]
  Placement = pos=(0,0,14) rot=(0,0,1;0rad)
FEATURE [Part::Fillet] Fillet015
  Base = -> Fillet014
  Edges = 1 edges r=5: [Edge3]
  Placement = pos=(-1,0,0) rot=(0,0,1;0rad)
FEATURE [Part::Box] Box027  label="Cube027"
  AttacherType = Attacher::AttachEngine3D
  Height = 2
  Length = 3
  Placement = pos=(8.5,-13,61) rot=(0,0,1;0rad)
  Width = 9
FEATURE [Part::Box] Box028  label="Cube028"
  AttacherType = Attacher::AttachEngine3D
  Height = 2
  Length = 3
  Placement = pos=(5.5,-13,61) rot=(0,0,1;0rad)
  Width = 9
FEATURE [Part::Sphere] Sphere009  label="Sphère009"
  Angle1 = -90
  Angle2 = 90
  Angle3 = 360
  AttacherType = Attacher::AttachEngine3D
  Placement = pos=(2,-28.5,47) rot=(0,0,1;0rad)
  Radius = 3
FEATURE [Part::Sphere] Sphere010  label="Sphère010"
  Angle1 = -90
  Angle2 = 90
  Angle3 = 360
  AttacherType = Attacher::AttachEngine3D
  Placement = pos=(17,-26,45) rot=(0,0,1;0rad)
  Radius = 4
FEATURE [Part::Sphere] Sphere011  label="Sphère011"
  Angle1 = -90
  Angle2 = 90
  Angle3 = 360
  AttacherType = Attacher::AttachEngine3D
  Placement = pos=(2,-28,45) rot=(0,0,1;0rad)
  Radius = 4
FEATURE [Part::Sphere] Sphere012  label="Sphère012"
  Angle1 = -90
  Angle2 = 90
  Angle3 = 360
  AttacherType = Attacher::AttachEngine3D
  Placement = pos=(17,-26.5,47) rot=(0,0,1;0rad)
  Radius = 3
FEATURE [Part::Cone] Cone015  label="Cône015"
  Angle = 360
  AttacherType = Attacher::AttachEngine3D
  Height = 29
  Placement = pos=(18,9,-12) rot=(1,0,0;0.506145rad)
  Radius1 = 4
  Radius2 = 7
FEATURE [Part::Sphere] Sphere013  label="Sphère013"
  Angle1 = -90
  Angle2 = 90
  Angle3 = 360
  AttacherType = Attacher::AttachEngine3D
  Placement = pos=(18,-5,14) rot=(0,0,1;0rad)
  Radius = 7
FEATURE [Part::Fuse] Fusion041
  Base = -> Cone015
  Placement = pos=(2,2,0) rot=(0,0,1;0rad)
  Tool = -> Sphere013
FEATURE [Part::Cone] Cone016  label="Cône016"
  Angle = 360
  AttacherType = Attacher::AttachEngine3D
  Height = 21
  Placement = pos=(20,11,-11) rot=(-1,0,0;0.244346rad)
  Radius1 = 4
  Radius2 = 3
FEATURE [Part::Sphere] Sphere014  label="Sphère014"
  Angle1 = -90
  Angle2 = 90
  Angle3 = 360
  AttacherType = Attacher::AttachEngine3D
  Placement = pos=(20,11,-11) rot=(0,0,1;0rad)
  Radius = 4.5
FEATURE [Part::Cylinder] Cylinder080  label="Cylindre076"
  Angle = 360
  AttacherType = Attacher::AttachEngine3D
  Height = 10
  Placement = pos=(2,37,-135) rot=(1,0,0;1.5708rad)
  Radius = 1.5
FEATURE [Part::Sphere] Sphere015  label="Sphère015"
  Angle1 = -90
  Angle2 = 90
  Angle3 = 360
  AttacherType = Attacher::AttachEngine3D
  Placement = pos=(2,37,-135) rot=(0,0,1;0rad)
  Radius = 1.5
FEATURE [Part::Sphere] Sphere016  label="Sphère016"
  Angle1 = -90
  Angle2 = 90
  Angle3 = 360
  AttacherType = Attacher::AttachEngine3D
  Placement = pos=(-1,37,-135) rot=(0,0,1;0rad)
  Radius = 1.5
FEATURE [Part::Sphere] Sphere017  label="Sphère017"
  Angle1 = -90
  Angle2 = 90
  Angle3 = 360
  AttacherType = Attacher::AttachEngine3D
  Placement = pos=(-4,37,-135) rot=(0,0,1;0rad)
  Radius = 1.5
FEATURE [Part::Sphere] Sphere018  label="Sphère018"
  Angle1 = -90
  Angle2 = 90
  Angle3 = 360
  AttacherType = Attacher::AttachEngine3D
  Placement = pos=(-8.15,35.5,-134.5) rot=(0,0,1;0rad)
  Radius = 1.5
FEATURE [Part::Cylinder] Cylinder081  label="Cylindre077"
  Angle = 360
  AttacherType = Attacher::AttachEngine3D
  Height = 10
  Placement = pos=(-5,26,-135) rot=(-0.948683,0,0.316228;1.62316rad)
  Radius = 1.5
FEATURE [Part::Box] Box029  label="Cube029"
  AttacherType = Attacher::AttachEngine3D
  Height = 2
  Length = 11
  Placement = pos=(-7,12,-136) rot=(0,0,1;0rad)
  Width = 22
FEATURE [Part::Box] Box030  label="Cube030"
  AttacherType = Attacher::AttachEngine3D
  Height = 10
  Length = 10
  Placement = pos=(-12,9,-144) rot=(0,0,1;0.279253rad)
  Width = 19
FEATURE [Part::Cylinder] Cylinder082  label="Cylindre078"
  Angle = 360
  AttacherType = Attacher::AttachEngine3D
  Height = 10
  Placement = pos=(-4,37,-135) rot=(1,0,0;1.5708rad)
  Radius = 1.5
FEATURE [Part::Cylinder] Cylinder083  label="Cylindre079"
  Angle = 360
  AttacherType = Attacher::AttachEngine3D
  Height = 10
  Placement = pos=(-1,37,-135) rot=(1,0,0;1.5708rad)
  Radius = 1.5
FEATURE [Part::Cut] Cut043
  Base = -> Box029
  Tool = -> Box030
FEATURE [Part::MultiFuse] Fusion042
  Placement = pos=(0,-9,-4) rot=(0,0,1;0rad)
  Shapes = -> [Cut043,Cylinder081,Sphere018,Cylinder082,Sphere017,Cylinder083,Sphere016,Cylinder080,Sphere015]
FEATURE [Part::Mirroring] Part__Mirroring004  label="Fusion040 (Mirror #4)001"
  Base = (1.90735e-06,12.3899,17.5186)
  Normal = (1,0,-1.19209e-07)
  Placement = pos=(20,-100,-64) rot=(1,0,0;2.05949rad)
  Source = -> Fusion042
FEATURE [Part::Fuse] Fusion043
  Base = -> Fusion041
  Tool = -> Sphere014
FEATURE [Part::Cylinder] Cylinder084  label="Cylindre080"
  Angle = 360
  AttacherType = Attacher::AttachEngine3D
  Height = 52
  Placement = pos=(0,19,-224) rot=(0,0,1;0rad)
  Radius = 2
FEATURE [Part::Cylinder] Cylinder085  label="Cylindre081"
  Angle = 360
  AttacherType = Attacher::AttachEngine3D
  Height = 101
  Placement = pos=(0,-6,-224) rot=(0,0,1;0rad)
  Radius = 2
FEATURE [Part::Fuse] Fusion046
  Base = -> Fusion024
  Tool = -> Cylinder084
FEATURE [Part::Mirroring] Part__Mirroring005  label="Cône016 (Mirror #6)"
  Base = (0,0,0)
  Normal = (1,0,0)
  Placement = pos=(20,0,0) rot=(0,0,1;0rad)
  Source = -> Cone016
FEATURE [Part::Mirroring] Part__Mirroring006  label="Fusion040 (Mirror #4)001 (Mirror #7)"
  Base = (0,0,0)
  Normal = (1,0,0)
  Placement = pos=(20,-2,2) rot=(0,0,1;0rad)
  Source = -> Part__Mirroring004
FEATURE [Part::Mirroring] Part__Mirroring007  label="Fusion043 (Mirror #8)"
  Base = (0,0,0)
  Normal = (1,0,0)
  Placement = pos=(20,0,0) rot=(0,0,1;0rad)
  Source = -> Fusion043
FEATURE [Part::Cone] Cone017  label="Cône017"
  Angle = 360
  AttacherType = Attacher::AttachEngine3D
  Height = 26
  Placement = pos=(8,-11,73) rot=(0,0,1;3.14159rad)
  Radius1 = 18
  Radius2 = 11
FEATURE [Part::Cone] Cone018  label="Cône018"
  Angle = 360
  AttacherType = Attacher::AttachEngine3D
  Height = 28
  Placement = pos=(8,-11,73) rot=(0,0,1;3.14159rad)
  Radius1 = 20
  Radius2 = 13
FEATURE [Part::Cut] Cut044
  Base = -> Cone018
  Placement = pos=(0,0,-12) rot=(0,0,1;0rad)
  Tool = -> Cone017
FEATURE [Part::Cylinder] Cylinder086  label="Cylindre082"
  Angle = 360
  AttacherType = Attacher::AttachEngine3D
  Height = 30
  Placement = pos=(8,-13,88) rot=(0,0,1;0rad)
  Radius = 2
FEATURE [Part::Fuse] Fusion047
  Base = -> Cut044
  Tool = -> Cylinder086
FEATURE [Drawing::FeatureViewPart] View
  Direction = (0,0,1)
  HiddenWidth = 0.15
  LineWidth = 0.35
  Rotation = 0
  ShowHiddenLines = false
  ShowSmoothLines = false
  Source = -> Cut011
  Tolerance = 0.05
  ViewResult = <g id="View"\n   transform="rotate(0,10,10) translate(10,10) scale(1,1)"\n  >\n<g   fill="none"\n   stroke="rgb(0, 0, 0)"\n   stroke-linecap="butt"\n   stroke-linejoin="miter"\n   stroke-width="0.350000"\n   transform="scale(1,-1)"\n  >\n<path d="M-41.5678 -8.85253 A42.5 42.5 0 0 1 41.5678 -8.85253" /><path d="M-39.7074 -8.1737 A45 45 0 0 1 39.7074 -8.1737" /><path d="M41.5678,-8.85253 C41.6182,-8.61926 41.5809,-8.36842 41.4647,-8.15994  C41.3497,-7.95075 41.157,-7.78593 40.9325,-7.70481  C40.7085,-7.6223 40.455,-7.62429 40.2323,-7.7103  C40.0091,-7.79492 39.819,-7.96276 39.7074,-8.1737 " /><path d="M-41.5678,-8.85253 C-41.6182,-8.61926 -41.5809,-8.36842 -41.4647,-8.15994  C-41.3497,-7.95075 -41.157,-7.78593 -40.9325,-7.70481  C-40.7085,-7.6223 -40.455,-7.62429 -40.2323,-7.7103  C-40.0091,-7.79492 -39.819,-7.96276 -39.7074,-8.1737 " /><circle cx ="18" cy ="-33" r ="3.5" /><path id= "6" d=" M -9.5 -39 L -9.5 -35 " />\n<path id= "7" d=" M -9.5 -35 L 9.5 -35 " />\n<path id= "8" d=" M -9.5 -39 L 9.5 -39 " />\n<path id= "9" d=" M 9.5 -39 L 9.5 -35 " />\n<circle cx ="-18" cy ="-33" r ="3.5" /></g>\n</g>
  Visible = false
  X = 10
  Y = 10
FEATURE [Drawing::FeatureViewPart] View001
  Direction = (0,0,1)
  HiddenWidth = 0.15
  LineWidth = 0.35
  Rotation = 0
  ShowHiddenLines = false
  ShowSmoothLines = false
  Source = -> Fusion021
  Tolerance = 0.05
  ViewResult = <blob: 11828 chars omitted>
  Visible = false
  X = 10
  Y = 10
FEATURE [Drawing::FeaturePage] Page
  EditableTexts = AUTHOR NAME | CREATION DATE | SUPERVISOR NAME | CHECK DATE | SCALE | WEIGHT | NUMBER | SHEET | TITLE | SUBTITLE
  Group = -> [View,View001]
  Template = /Applications/FreeCAD.app/Contents/Resources/data/Mod/Drawing/Templates/A3_Landscape.svg
